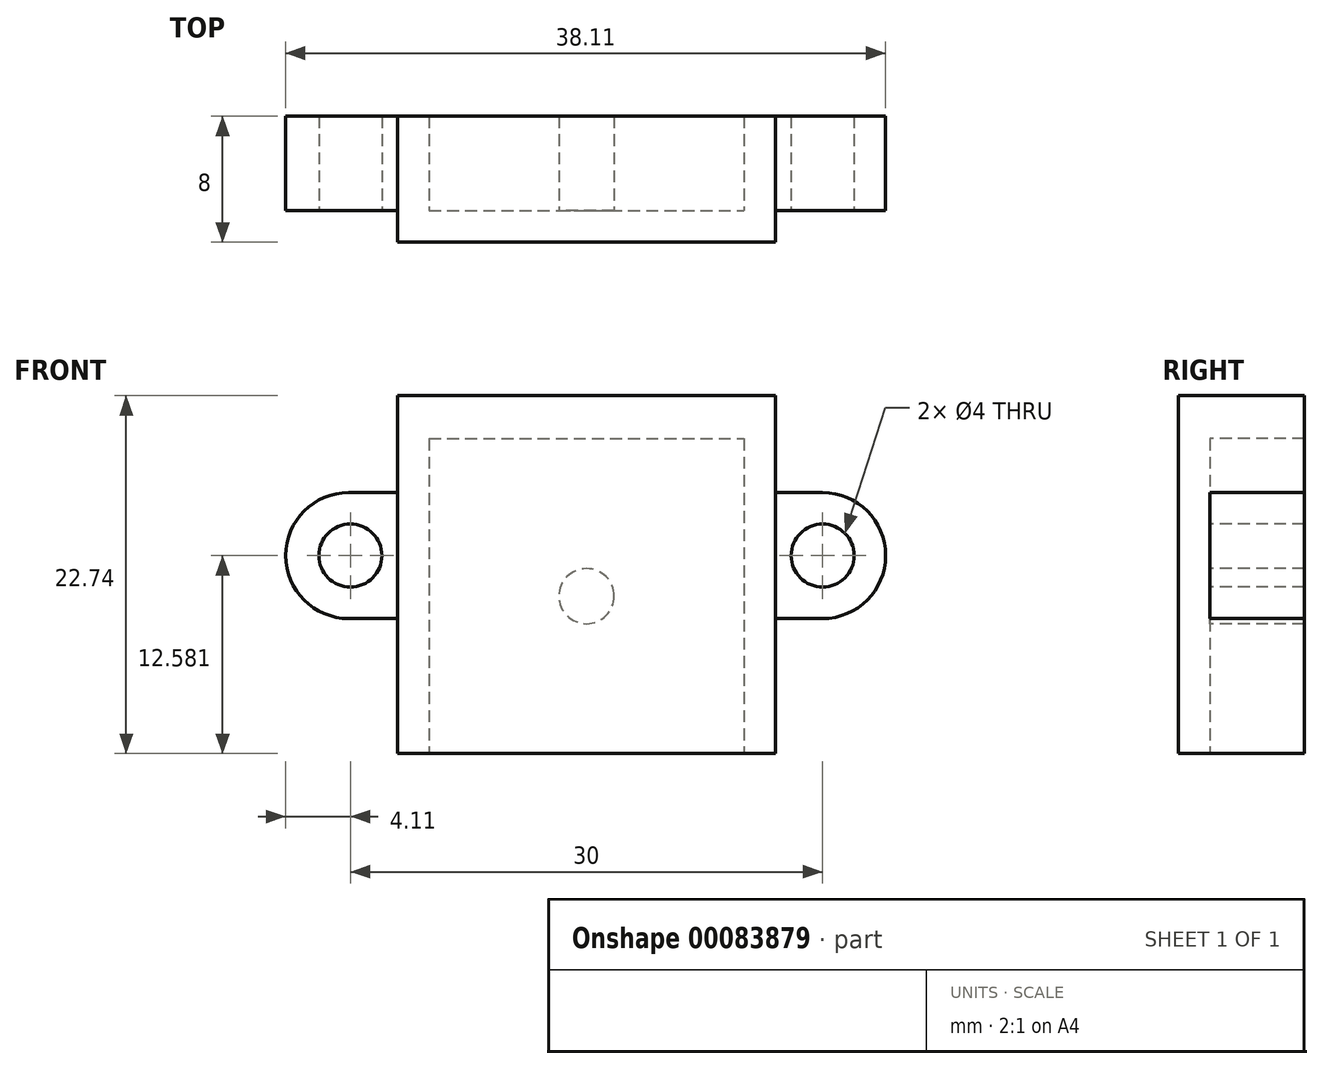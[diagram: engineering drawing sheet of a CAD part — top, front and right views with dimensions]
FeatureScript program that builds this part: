
annotation { "Feature Type Name" : "Feature", "Feature Type Description" : "" }
export const myFeature = defineFeature(function(context is Context, id is Id, definition is map)
    precondition{}
    {
        {
            var Q0;
            Q0=qCreatedBy(makeId("Front.planeOp"),FACE);
            var sketch = newSketch(context, id + "F0", { "sketchPlane" : qUnion([Q0])});
            skLineSegment(sketch, "E0.bottom", {"start": v(-29, 25.73) * mm, "end": v(-9, 25.73) * mm});
            skLineSegment(sketch, "E0.top", {"start": v(-31, 5.73) * mm, "end": v(-29, 5.73) * mm});
            skLineSegment(sketch, "E0.left", {"start": v(-29, 25.73) * mm, "end": v(-29, 5.73) * mm});
            skLineSegment(sketch, "E0.right", {"start": v(-9, 25.73) * mm, "end": v(-9, 5.73) * mm});
            skPoint(sketch, "E1", {"position": v(-19, 15.73) * mm});
            skCircle(sketch, "E2", {"center": v(-19, 15.73) * mm, "radius": 1.75 * mm});
            skLineSegment(sketch, "E3", {"start": v(-29, 5.73) * mm, "end": v(-9, 5.73) * mm});
            skLineSegment(sketch, "E4", {"start": v(-31, 5.73) * mm, "end": v(-31, 22.31) * mm});
            skLineSegment(sketch, "E5", {"start": v(-31, 28.47) * mm, "end": v(-7, 28.47) * mm});
            skLineSegment(sketch, "E6", {"start": v(-7, 28.47) * mm, "end": v(-7, 5.73) * mm});
            skCircle(sketch, "E7", {"center": v(-34, 18.31) * mm, "radius": 2 * mm});
            skCircle(sketch, "E8", {"center": v(-4, 18.31) * mm, "radius": 2 * mm});
            skLineSegment(sketch, "E9.top", {"start": v(-31, 14.31) * mm, "end": v(-34.1, 14.31) * mm});
            skLineSegment(sketch, "E9.left", {"start": v(-31, 22.31) * mm, "end": v(-31, 14.31) * mm});
            skLineSegment(sketch, "E9.right", {"start": v(-38.1, 18.31) * mm, "end": v(-38.1, 18.31) * mm});
            skLineSegment(sketch, "E10", {"start": v(-31, 22.31) * mm, "end": v(-34.1, 22.31) * mm});
            skLineSegment(sketch, "E11", {"start": v(-31, 22.31) * mm, "end": v(-31, 28.47) * mm});
            skArc(sketch, "E12.filletArc", {"start": v(-34.1, 22.31) * mm, "mid": v(-38.1, 18.31) * mm, "end": v(-34.1, 14.31) * mm});
            skLineSegment(sketch, "E13", {"start": v(-4, 22.31) * mm, "end": v(-7, 22.31) * mm});
            skLineSegment(sketch, "E14", {"start": v(-4, 14.31) * mm, "end": v(-7, 14.31) * mm});
            skArc(sketch, "E15", {"start": v(0, 18.31) * mm, "mid": v(-1.17, 21.14) * mm, "end": v(-4, 22.31) * mm});
            skArc(sketch, "E16", {"start": v(-4, 14.31) * mm, "mid": v(-1.17, 15.48) * mm, "end": v(0, 18.31) * mm});
            skLineSegment(sketch, "E17", {"start": v(-9, 5.73) * mm, "end": v(-7, 5.73) * mm});
            skLineSegment(sketch, "E18", {"start": v(-29, 5.73) * mm, "end": v(-29, 5.73) * mm});
            skSolve(sketch);
        }
        {
            var Q0;
            Q0=makeQuery(id+"F0.imprint","IMPRINT",FACE,{"disambiguationData":[TD([[makeQuery(id+"F0.imprint","IMPRINT",EDGE,{"derivedFrom":sQuery(id+"F0.wireOp",EDGE,"E0.bottom")}),1.0]])]});
            var Q1;
            {var subQ0=sQuery(id+"F0.wireOp",EDGE,"E0.left");Q1=makeQuery(id+"F0.imprint","IMPRINT",FACE,{"disambiguationData":[TD([[makeQuery(id+"F0.imprint","IMPRINT",EDGE,{"derivedFrom":subQ0}),1.0]])]});}
            var Q2;
            {var subQ0=sQuery(id+"F0.wireOp",EDGE,"E0.bottom");Q2=makeQuery(id+"F0.imprint","IMPRINT",FACE,{"disambiguationData":[TD([[makeQuery(id+"F0.imprint","IMPRINT",EDGE,{"derivedFrom":subQ0}),-1.0]])]});}
            var Q3;
            {var subQ0=sQuery(id+"F0.wireOp",EDGE,"E0.right");Q3=makeQuery(id+"F0.imprint","IMPRINT",FACE,{"disambiguationData":[TD([[makeQuery(id+"F0.imprint","IMPRINT",EDGE,{"derivedFrom":subQ0}),-1.0]])]});}
            var Q4;
            {var subQ1=sQuery(id+"F0.wireOp",EDGE,"lwsroQam-fsN0-LR1t-fIe1-Hg1vca0ca4ya");var subQ3=sQuery(id+"F0.wireOp",EDGE,"E2");var subQ4=makeQuery(id+"F0.imprint","INTERSECT",VERTEX,{"disambiguationData":[OD(1.0)],"derivedFrom":[subQ1,subQ3]});Q4=makeQuery(id+"F0.imprint","IMPRINT",FACE,{"disambiguationData":[TD([[makeQuery(id+"F0.imprint","IMPRINT",EDGE,{"disambiguationData":[TD([[subQ4,1.0]])],"derivedFrom":subQ3}),-1.0]])]});}
            var Q5;
            {var subQ0=sQuery(id+"F0.wireOp",EDGE,"MSVRqUWr-FRsP-cjvw-Ge6F-E8IThWNg6tYz");var subQ1=sQuery(id+"F0.wireOp",EDGE,"lwsroQam-fsN0-LR1t-fIe1-Hg1vca0ca4ya");var subQ2=makeQuery(id+"F0.imprint","INTERSECT",VERTEX,{"derivedFrom":[subQ1,subQ0]});Q5=makeQuery(id+"F0.imprint","IMPRINT",FACE,{"disambiguationData":[TD([[makeQuery(id+"F0.imprint","IMPRINT",EDGE,{"disambiguationData":[TD([[subQ2,-1.0]])],"derivedFrom":subQ1}),-1.0]])]});}
            var Q6;
            {var subQ0=sQuery(id+"F0.wireOp",EDGE,"E2");var subQ1=sQuery(id+"F0.wireOp",EDGE,"lwsroQam-fsN0-LR1t-fIe1-Hg1vca0ca4ya");var subQ2=makeQuery(id+"F0.imprint","INTERSECT",VERTEX,{"disambiguationData":[OD(0.0)],"derivedFrom":[subQ1,subQ0]});Q6=makeQuery(id+"F0.imprint","IMPRINT",FACE,{"disambiguationData":[TD([[makeQuery(id+"F0.imprint","IMPRINT",EDGE,{"disambiguationData":[TD([[subQ2,-1.0]])],"derivedFrom":subQ1}),-1.0]])]});}
            var Q7;
            {var subQ0=sQuery(id+"F0.wireOp",EDGE,"E2");var subQ1=sQuery(id+"F0.wireOp",EDGE,"lwsroQam-fsN0-LR1t-fIe1-Hg1vca0ca4ya");var subQ2=makeQuery(id+"F0.imprint","INTERSECT",VERTEX,{"disambiguationData":[OD(0.0)],"derivedFrom":[subQ1,subQ0]});Q7=makeQuery(id+"F0.imprint","IMPRINT",FACE,{"disambiguationData":[TD([[makeQuery(id+"F0.imprint","IMPRINT",EDGE,{"disambiguationData":[TD([[subQ2,-1.0]])],"derivedFrom":subQ1}),1.0]])]});}
            var Q8;
            {var subQ0=sQuery(id+"F0.wireOp",EDGE,"MSVRqUWr-FRsP-cjvw-Ge6F-E8IThWNg6tYz");var subQ1=sQuery(id+"F0.wireOp",EDGE,"lwsroQam-fsN0-LR1t-fIe1-Hg1vca0ca4ya");var subQ2=makeQuery(id+"F0.imprint","INTERSECT",VERTEX,{"derivedFrom":[subQ1,subQ0]});Q8=makeQuery(id+"F0.imprint","IMPRINT",FACE,{"disambiguationData":[TD([[makeQuery(id+"F0.imprint","IMPRINT",EDGE,{"disambiguationData":[TD([[subQ2,-1.0]])],"derivedFrom":subQ1}),1.0]])]});}
            var Q9;
            Q9=makeQuery(id+"F0.imprint","IMPRINT",FACE,{"disambiguationData":[TD([[makeQuery(id+"F0.imprint","IMPRINT",EDGE,{"derivedFrom":sQuery(id+"F0.wireOp",EDGE,"E2")}),1.0]])]});
            extrude(context, id + "F1", {"entities" : qUnion([Q0, Q1, Q2, Q3, Q4, Q5, Q6, Q7, Q8, Q9]), "depth" : 2 * mm});
        }
        {
            var Q0;
            Q0=makeQuery(id+"F0.imprint","IMPRINT",FACE,{"disambiguationData":[TD([[makeQuery(id+"F0.imprint","IMPRINT",EDGE,{"derivedFrom":sQuery(id+"F0.wireOp",EDGE,"E0.bottom")}),1.0]])]});
            var Q1;
            Q1=makeQuery(id+"F0.imprint","IMPRINT",FACE,{"disambiguationData":[TD([[makeQuery(id+"F0.imprint","IMPRINT",EDGE,{"derivedFrom":sQuery(id+"F0.wireOp",EDGE,"E8")}),-1.0]])]});
            var Q2;
            Q2=makeQuery(id+"F0.imprint","IMPRINT",FACE,{"disambiguationData":[TD([[makeQuery(id+"F0.imprint","IMPRINT",EDGE,{"derivedFrom":sQuery(id+"F0.wireOp",EDGE,"E2")}),1.0]])]});
            var Q3;
            Q3=makeQuery(id+"F0.imprint","IMPRINT",FACE,{"disambiguationData":[TD([[makeQuery(id+"F0.imprint","IMPRINT",EDGE,{"derivedFrom":sQuery(id+"F0.wireOp",EDGE,"E7")}),-1.0]])]});
            extrude(context, id + "F2", {"entities" : qUnion([Q0, Q1, Q2, Q3]), "operationType" : NewBodyOperationType.ADD, "oppositeDirection" : true, "depth" : 6 * mm});
        }
    });
